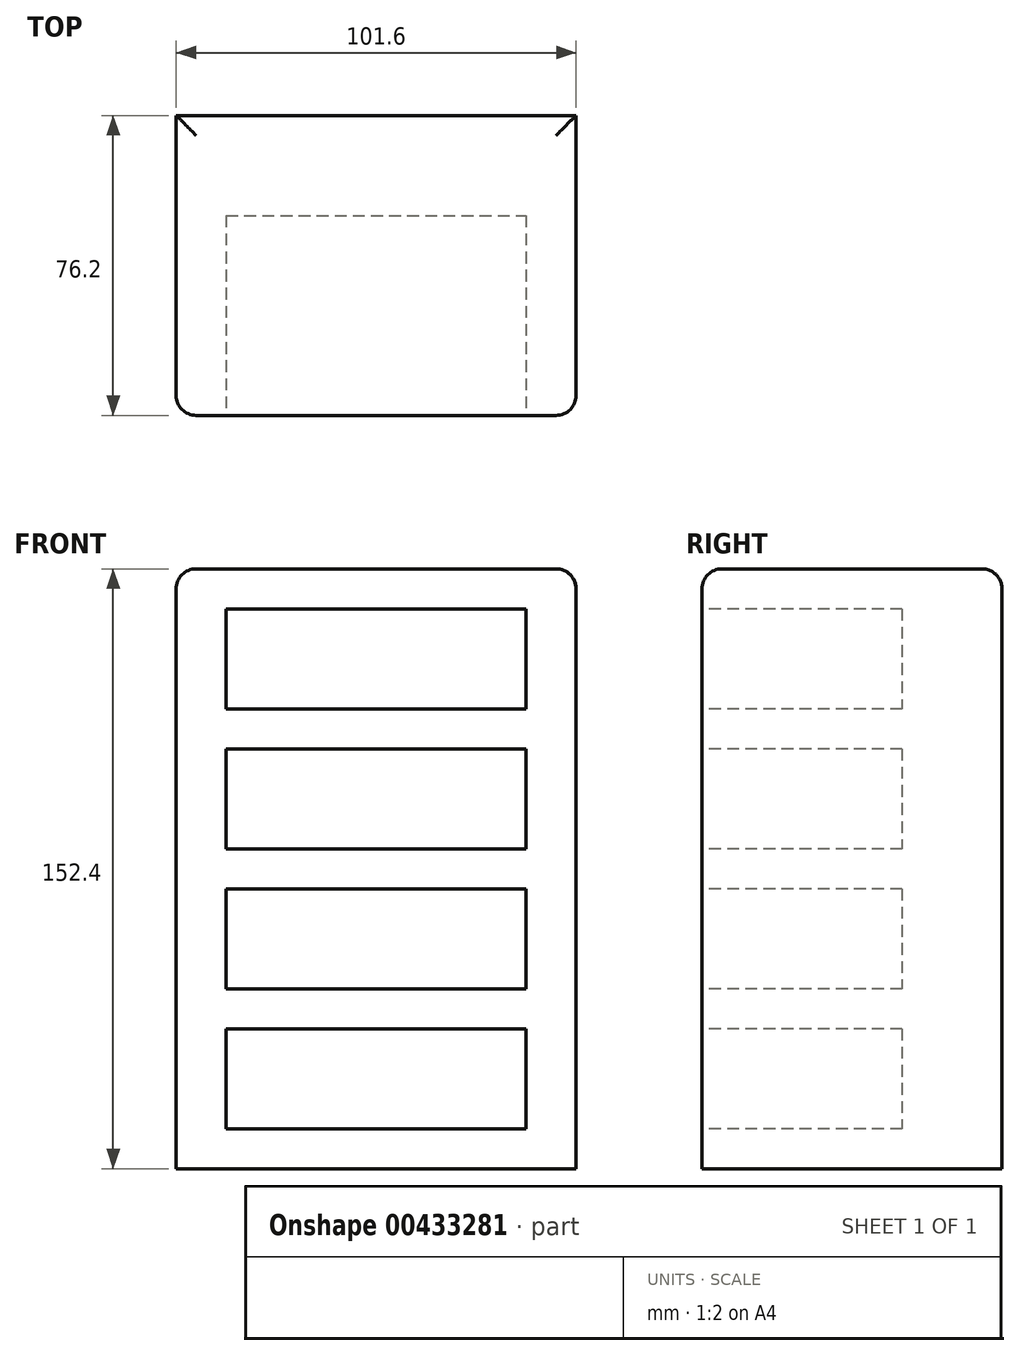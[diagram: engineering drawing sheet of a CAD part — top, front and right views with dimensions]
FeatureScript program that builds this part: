
annotation { "Feature Type Name" : "Feature", "Feature Type Description" : "" }
export const myFeature = defineFeature(function(context is Context, id is Id, definition is map)
    precondition{}
    {
        {
            var Q0;
            Q0=qCreatedBy(makeId("Top.planeOp"),FACE);
            var sketch = newSketch(context, id + "F0", { "sketchPlane" : qUnion([Q0])});
            skLineSegment(sketch, "E0.bottom", {"start": v(0, 0) * mm, "end": v(101.6, 0) * mm});
            skLineSegment(sketch, "E0.top", {"start": v(0, 76.2) * mm, "end": v(101.6, 76.2) * mm});
            skLineSegment(sketch, "E0.left", {"start": v(0, 0) * mm, "end": v(0, 76.2) * mm});
            skLineSegment(sketch, "E0.right", {"start": v(101.6, 0) * mm, "end": v(101.6, 76.2) * mm});
            skSolve(sketch);
        }
        {
            var Q0;
            Q0=makeQuery(id+"F0.imprint","IMPRINT",FACE,{"disambiguationData":[TD([[makeQuery(id+"F0.imprint","IMPRINT",EDGE,{"derivedFrom":sQuery(id+"F0.wireOp",EDGE,"E0.bottom")}),1.0]])]});
            extrude(context, id + "F1", {"entities" : qUnion([Q0]), "depth" : 152.4 * mm});
        }
        {
            var Q0;
            Q0=makeQuery(id+"F1.opExtrude","SWEPT_FACE",FACE,{"disambiguationData":[OSD([sQuery(id+"F0.wireOp",EDGE,"E0.bottom")])]});
            var sketch = newSketch(context, id + "F2", { "sketchPlane" : qUnion([Q0])});
            skLineSegment(sketch, "E1.bottom", {"start": v(12.7, 142.24) * mm, "end": v(88.9, 142.24) * mm});
            skLineSegment(sketch, "E1.top", {"start": v(12.7, 116.84) * mm, "end": v(88.9, 116.84) * mm});
            skLineSegment(sketch, "E1.left", {"start": v(12.7, 142.24) * mm, "end": v(12.7, 116.84) * mm});
            skLineSegment(sketch, "E1.right", {"start": v(88.9, 142.24) * mm, "end": v(88.9, 116.84) * mm});
            skLineSegment(sketch, "E2.0.1.0", {"start": v(12.7, 106.68) * mm, "end": v(12.7, 81.28) * mm});
            skLineSegment(sketch, "E2.0.1.1", {"start": v(12.7, 106.68) * mm, "end": v(88.9, 106.68) * mm});
            skLineSegment(sketch, "E2.0.1.2", {"start": v(12.7, 81.28) * mm, "end": v(88.9, 81.28) * mm});
            skLineSegment(sketch, "E2.0.1.3", {"start": v(88.9, 106.68) * mm, "end": v(88.9, 81.28) * mm});
            skLineSegment(sketch, "E2.0.2.0", {"start": v(12.7, 71.12) * mm, "end": v(12.7, 45.72) * mm});
            skLineSegment(sketch, "E2.0.2.1", {"start": v(12.7, 71.12) * mm, "end": v(88.9, 71.12) * mm});
            skLineSegment(sketch, "E2.0.2.2", {"start": v(12.7, 45.72) * mm, "end": v(88.9, 45.72) * mm});
            skLineSegment(sketch, "E2.0.2.3", {"start": v(88.9, 71.12) * mm, "end": v(88.9, 45.72) * mm});
            skLineSegment(sketch, "E2.0.3.0", {"start": v(12.7, 35.56) * mm, "end": v(12.7, 10.16) * mm});
            skLineSegment(sketch, "E2.0.3.1", {"start": v(12.7, 35.56) * mm, "end": v(88.9, 35.56) * mm});
            skLineSegment(sketch, "E2.0.3.2", {"start": v(12.7, 10.16) * mm, "end": v(88.9, 10.16) * mm});
            skLineSegment(sketch, "E2.0.3.3", {"start": v(88.9, 35.56) * mm, "end": v(88.9, 10.16) * mm});
            skLineSegment(sketch, "E2.direction1", {"start": v(12.7, 116.84) * mm, "end": v(38.1, 116.84) * mm, "construction": true});
            skLineSegment(sketch, "E2.direction2", {"start": v(12.7, 116.84) * mm, "end": v(12.7, 81.28) * mm, "construction": true});
            skSolve(sketch);
        }
        {
            var Q0;
            Q0 = qSketchRegion(id + "F2", true);
            extrude(context, id + "F3", {"entities" : qUnion([Q0]), "operationType" : NewBodyOperationType.REMOVE, "oppositeDirection" : true, "depth" : 50.8 * mm});
        }
        {
            var Q0;
            Q0=makeQuery(id+"F1.opExtrude","CAP_EDGE",EDGE,{"disambiguationData":[OSD([sQuery(id+"F0.wireOp",EDGE,"E0.right")])],"isStart":false});
            var Q1;
            Q1=makeQuery(id+"F1.opExtrude","CAP_EDGE",EDGE,{"disambiguationData":[OSD([sQuery(id+"F0.wireOp",EDGE,"E0.left")])],"isStart":false});
            var Q2;
            Q2=makeQuery(id+"F1.opExtrude","CAP_EDGE",EDGE,{"disambiguationData":[OSD([sQuery(id+"F0.wireOp",EDGE,"E0.bottom")])],"isStart":false});
            var Q3;
            Q3=makeQuery(id+"F1.opExtrude","CAP_EDGE",EDGE,{"disambiguationData":[OSD([sQuery(id+"F0.wireOp",EDGE,"E0.top")])],"isStart":false});
            var Q4;
            Q4=makeQuery(id+"F1.opExtrude","SWEPT_EDGE",EDGE,{"disambiguationData":[OSD([sQuery(id+"F0.wireOp",EDGE,"E0.bottom"),sQuery(id+"F0.wireOp",EDGE,"E0.right")])]});
            var Q5;
            Q5=makeQuery(id+"F1.opExtrude","SWEPT_EDGE",EDGE,{"disambiguationData":[OSD([sQuery(id+"F0.wireOp",EDGE,"E0.bottom"),sQuery(id+"F0.wireOp",EDGE,"E0.left")])]});
            fillet(context, id + "F4", {"entities" : qUnion([Q0, Q1, Q2, Q3, Q4, Q5]), "radius" : 5.08 * mm, "tangentPropagation" : true, "allowEdgeOverflow" : false});
        }
    });
